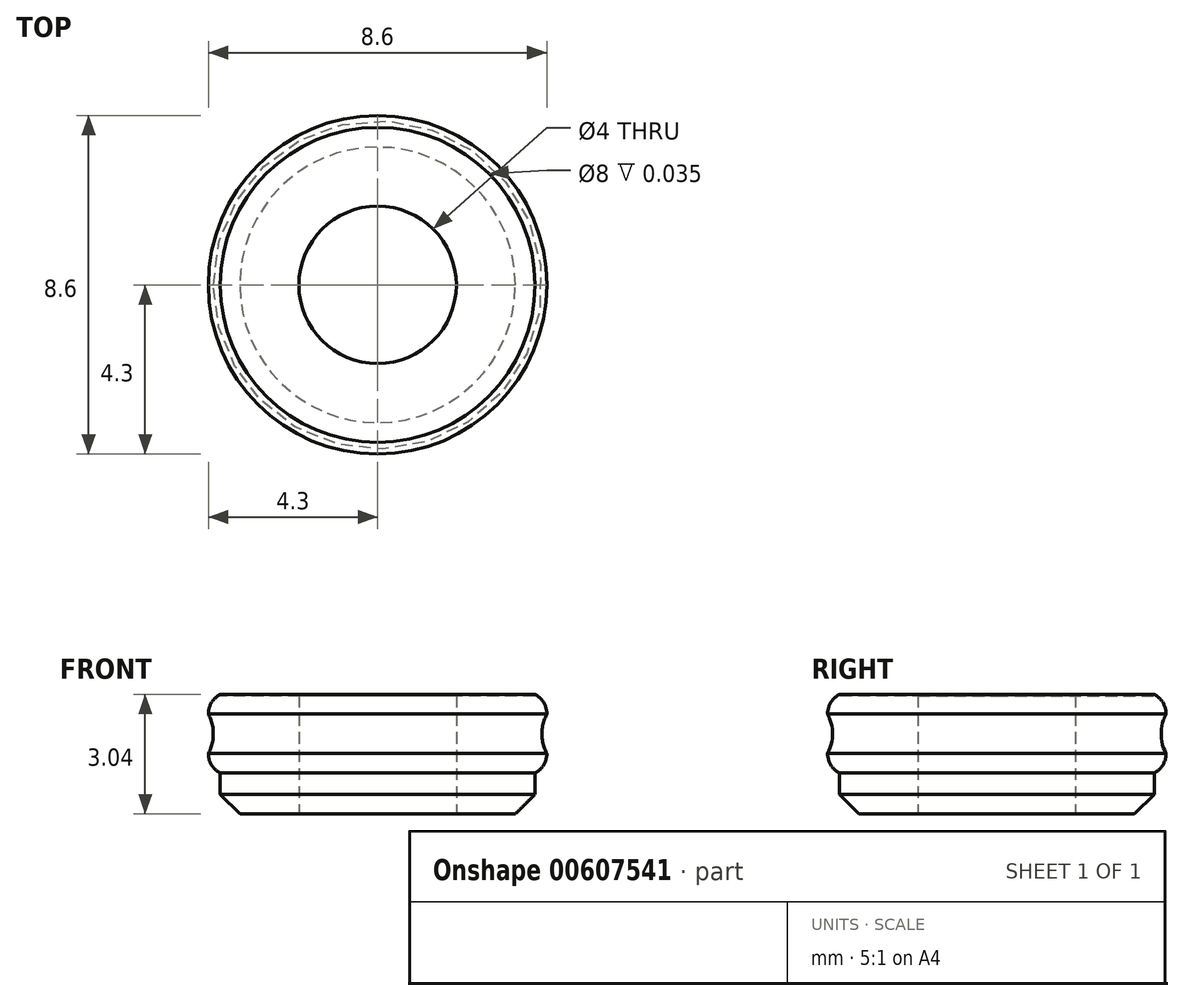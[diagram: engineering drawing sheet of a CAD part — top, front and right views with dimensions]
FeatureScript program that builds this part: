
annotation { "Feature Type Name" : "Feature", "Feature Type Description" : "" }
export const myFeature = defineFeature(function(context is Context, id is Id, definition is map)
    precondition{}
    {
        {
            var Q0;
            Q0=qCreatedBy(makeId("Top.planeOp"),FACE);
            var sketch = newSketch(context, id + "F0", { "sketchPlane" : qUnion([Q0])});
            skCircle(sketch, "E0", {"center": v(0, 0) * mm, "radius": 2 * mm});
            skCircle(sketch, "E1", {"center": v(0, 0) * mm, "radius": 4 * mm});
            skSolve(sketch);
        }
        {
            var Q0;
            Q0=makeQuery(id+"F0.imprint","IMPRINT",FACE,{"disambiguationData":[TD([[makeQuery(id+"F0.imprint","IMPRINT",EDGE,{"derivedFrom":sQuery(id+"F0.wireOp",EDGE,"E0")}),-1.0]])]});
            extrude(context, id + "F1", {"entities" : qUnion([Q0]), "depth" : 3 * mm, "offsetDistance" : 25 * mm});
        }
        {
            var Q0;
            Q0=qCreatedBy(makeId("Front.planeOp"),FACE);
            var sketch = newSketch(context, id + "F2", { "sketchPlane" : qUnion([Q0])});
            skLineSegment(sketch, "E2", {"start": v(0, -1.5) * mm, "end": v(0, 6) * mm, "construction": true});
            skLineSegment(sketch, "E3", {"start": v(-4, 0) * mm, "end": v(-4, 4.07) * mm, "construction": true});
            skLineSegment(sketch, "E4", {"start": v(4, 4) * mm, "end": v(4, 0) * mm, "construction": true});
            skPoint(sketch, "E5", {"position": v(-4, 2.04) * mm});
            skPoint(sketch, "E6.right.end.orphan", {"position": v(-3.7, 1.54) * mm});
            skPoint(sketch, "E6.right.start.orphan", {"position": v(-3.7, 2.54) * mm});
            skArc(sketch, "E7", {"start": v(-4.3, 2.54) * mm, "mid": v(-4.22, 2.83) * mm, "end": v(-4, 3.04) * mm});
            skLineSegment(sketch, "E8", {"start": v(-4, 2.04) * mm, "end": v(-5.35, 2.04) * mm, "construction": true});
            skArc(sketch, "E9.MirrorCS", {"start": v(-4.3, 1.54) * mm, "mid": v(-4.22, 1.24) * mm, "end": v(-4, 1.04) * mm});
            skPoint(sketch, "E6.bottom.end.orphan", {"position": v(-4, 2.54) * mm});
            skArc(sketch, "E10", {"start": v(-4.3, 1.54) * mm, "mid": v(-4.17, 2.04) * mm, "end": v(-4.3, 2.54) * mm});
            skPoint(sketch, "E10.third.point", {"position": v(-4.17, 2.04) * mm});
            skLineSegment(sketch, "E11", {"start": v(-4, 3.04) * mm, "end": v(-4, 1.04) * mm});
            skSolve(sketch);
        }
        {
            var Q0;
            Q0 = qSketchRegion(id + "F2", true);
            var Q1;
            Q1=sQuery(id+"F2.wireOp",EDGE,"E2");
            revolve(context, id + "F3", {"operationType" : NewBodyOperationType.ADD, "entities" : qUnion([Q0]), "axis" : qUnion([Q1]), "revolveType" : RevolveType.FULL});
        }
        {
            var Q0;
            Q0=makeQuery(id+"F1.opExtrude","CAP_EDGE",EDGE,{"disambiguationData":[OSD([sQuery(id+"F0.wireOp",EDGE,"E1")])],"isStart":false});
            var Q1;
            Q1=makeQuery(id+"F1.opExtrude","CAP_EDGE",EDGE,{"disambiguationData":[OSD([sQuery(id+"F0.wireOp",EDGE,"E1")])],"isStart":true});
            chamfer(context, id + "F4", {"entities" : qUnion([Q0, Q1]), "width" : 0.5 * mm, "tangentPropagation" : true});
        }
    });
